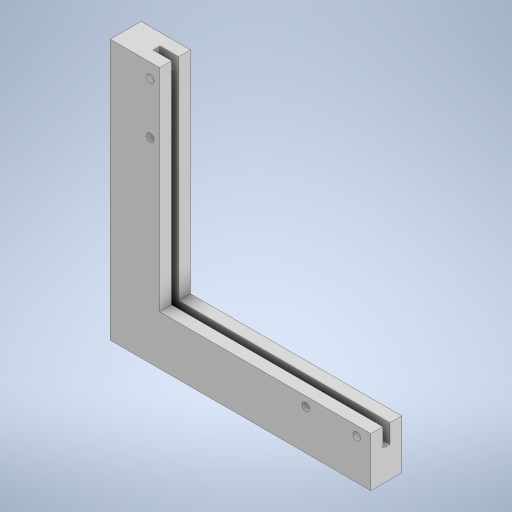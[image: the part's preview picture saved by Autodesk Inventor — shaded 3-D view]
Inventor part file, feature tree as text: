
AUTODESK INVENTOR PART (.ipt)
format: ipt  version: 2024 (Build 280153000, 153)  size: 354,816 bytes
history: native  units: mm
features: projected_geometry x8, extrude x6, sketch x6
ambient origin geometry x8: Origin, YZ Plane, XZ Plane, XY Plane, X Axis, Y Axis, Z Axis, Center Point
bodies: Solid1 (feature_tree)
feature tree (20):
  extrude  "Extrusion1"  Depth=10.0mm
  extrude  "Extrusion2"  Depth=6.0mm
  extrude  "Extrusion5"  Depth=6.0mm
  extrude  "Extrusion6"  Depth=2.5mm
  extrude  "Extrusion7"  Depth=6.0mm
  extrude  "Extrusion8"  Depth=10.0mm
  sketch  "Sketch1"  dims[d0=68.5mm d1=10.0mm]
  sketch  "Sketch2"  dims[d2=10.0mm d3=6.0mm]
  projected_geometry  "Projected Loop1"
  sketch  "Sketch5"  dims[d6=10.0mm d7=6.0mm]
  projected_geometry  "Projected Loop6"
  projected_geometry  "Projected Loop7"
  sketch  "Sketch6"  dims[d8=0.0mm d9=2.5mm]
  projected_geometry  "Projected Loop8"
  projected_geometry  "Projected Loop9"
  sketch  "Sketch7"  dims[d11=6.0mm d13=69.9mm]
  projected_geometry  "Projected Loop10"
  projected_geometry  "Projected Loop11"
  sketch  "Sketch8"  dims[d14=2.5mm d15=53.4mm d16=0.0mm d17=84.5mm d18=20.0mm d20=90.0deg d22=3.875mm d23=0.0mm d24=10.0mm d25=10.0mm d26=2.25mm d27=0.0mm d49=3.875mm d50=0.0mm d51=4.0mm d52=4.0mm d53=10.0mm d54=5.0mm d55=5.0mm d58=10.0mm d59=0.0mm d60=4.0mm d61=4.0mm d62=10.0mm d63=5.0mm d64=5.0mm d67=10.0mm d68=0.0mm d69=10.0mm d70=0.0mm d73=24.0mm d74=34.25mm d77=28.0mm d78=34.25mm]
  projected_geometry  "Projected Loop12"
